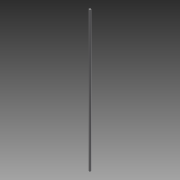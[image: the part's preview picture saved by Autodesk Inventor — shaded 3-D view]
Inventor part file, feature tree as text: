
AUTODESK INVENTOR PART (.ipt)
format: ipt  version: 2015 SP1 (Build 190203100, 203)  size: 64,000 bytes
history: native  units: mm
features: extrude x1, sketch x1
ambient origin geometry x8: Origin, YZ Plane, XZ Plane, XY Plane, X Axis, Y Axis, Z Axis, Center Point
bodies: Solid1 (feature_tree)
feature tree (2):
  extrude  "Extrusion1"  Depth=609.6mm TaperAngle=0.0deg
  sketch  "Sketch1"  dims[d0=8.0mm d1=609.6mm d2=0.0mm]
